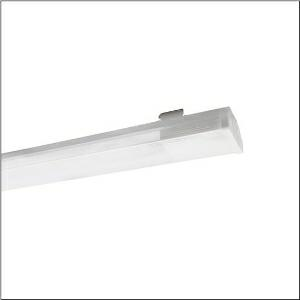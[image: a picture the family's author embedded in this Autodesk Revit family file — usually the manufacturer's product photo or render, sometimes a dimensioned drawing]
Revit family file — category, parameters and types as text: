
# Revit family: modario_r__31_gen_2_53bm8137u4l3d2_98c8
name_source: partatom
category: Lighting Fixtures
units: mm (PartAtom-declared; Revit-internal decimal feet)

## family parameters
Cut with Voids When Loaded = No
Host = Face
Light Source = No
Part Type = Normal
Room Calculation Point = No
Round Connector Dimension = Use Diameter
Shared = No

## types (1)
- Modario® 31 Gen.2 (1 x LED, 23060 lm, 126 W, 4000K)
    Apparent Load = 126 VA
    CIE Flux Codes = 62 83 95 93 100
    Color Rendering = 80
    Color Temperature = 4000K
    Default Elevation = 1800 mm
    Description = Modario® 31 Gen.2, luminaire insert, of sheet steel, coil coated, white, length: 2.392mm, width: 81mm, height: 82mm, 8x system unit, system units: 299mm, LED rated luminous flux: 23.060lm, light colour: 840, control gear: ON/OFF, with plug, 3-pole, with phase selection, mains connection: 220..240V, AC, 50/60Hz, rated input power: 126W, through-wiring accessed according to module size, primary optical cover: cover, of PMMA, light emission: direct distribution, primary light characteristic: symmetric, protection rating (complete): IP20, protection rating (LED compartment): IP50, insulation class (complete): insulation class I (protective earthing), certification: CE, ENEC, VDE, UKCA, impact resistance: IK03, permissible ambient temperature for indoor applications: -40..+35°C, corresponds to IFS (International Featured Standards) requirements for safety and quality in the food industry, reducing of maximum allowable ambient temperature of 5°C with ceiling mounting, packaging unit: 1 piece
    Height = 92 mm
    Lamp = 1 x LED
    Lamp Light Flux = 23060 lm
    Lamp Power = 126 W
    Lamp count = 1
    Length = 2392 mm
    Luminous efficacy = 183 lm/W
    Manufacturer = Siteco
    ModVariant = No
    Model = 53BM8137U4L3D2
    Mounting Place = Ceiling
    Mounting Type = Pendant
    Number of Poles = 1
    OnlyDefault = Yes
    Power Factor = 1
    Product Name = Modario® 31 Gen.2
    Product group = luminaire insert | ceiling pendant
    ProductGroupID = 902
    Protection Class = Protection class I
    Protection Degree = IP 20
    RLX_Detail_Level = 1
    RLX_Emergency_Light_Flux = 0 lm
    RLX_Emergency_Type = 0
    RLX_Emergency_Type_DB = No
    RlxData = <blob elided: 34777 chars, md5=1685a4df>
    Socket = socket
    Standby Power = 0 W
    System Light Flux = 23061 lm
    System Power = 126 W
    Type Comments = Product without accessories
    Type Image = l_1341883.jpg
    URL = http://relux.com
    VarID = ---
    Voltage = 0 V
    Weight = 0.00 kg
    Width = 81 mm

## geometry (parser evidence)
native form markers: Blend x4, Sweep x13
no freeform markers — native parametric forms only
